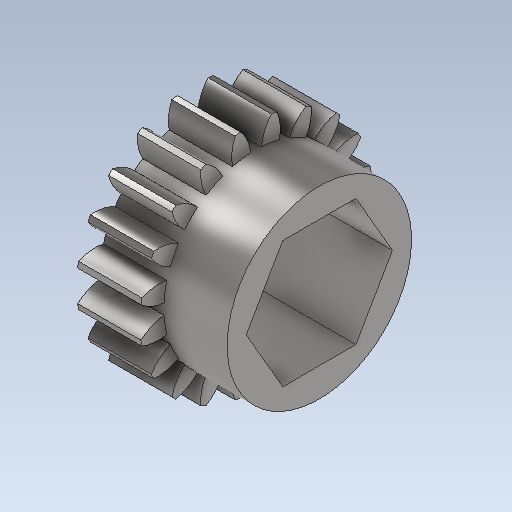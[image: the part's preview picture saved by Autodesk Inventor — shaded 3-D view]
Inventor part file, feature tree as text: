
AUTODESK INVENTOR PART (.ipt)
format: ipt  version: 2023 (Build 270158000, 158)  size: 339,456 bytes
history: native  units: in
note: dims shown in document units (in); Inventor stores cm internally (conversion verified against a paired STEP export)
features: other x3, sketch x2
ambient origin geometry x8: Origin, YZ Plane, XZ Plane, XY Plane, X Axis, Y Axis, Z Axis, Center Point
bodies: Solid1 (feature_tree)
feature tree (5):
  other  "CH-1-01-20T_Idler.ipt"
  other  "Solid1::CH-1-01-20T_Idler.ipt"
  other  "TaggingFeature1"
  sketch  "Sketch3"  dims[d0=0.3937in]
  sketch  "Sketch4"
